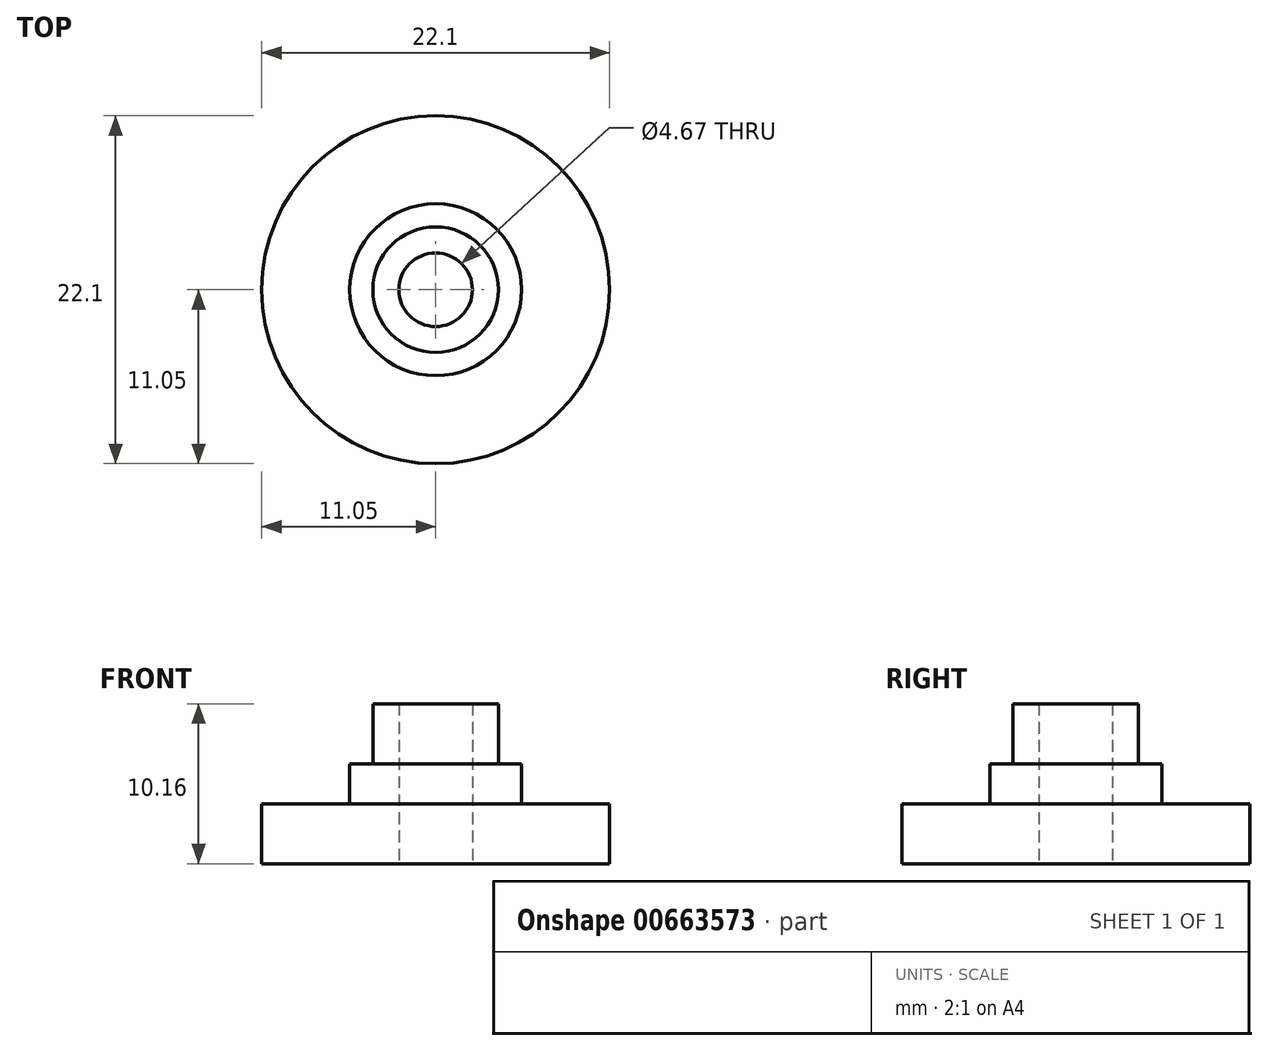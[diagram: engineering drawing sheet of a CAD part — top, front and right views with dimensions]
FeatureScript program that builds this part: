
annotation { "Feature Type Name" : "Feature", "Feature Type Description" : "" }
export const myFeature = defineFeature(function(context is Context, id is Id, definition is map)
    precondition{}
    {
        {
            var Q0;
            Q0=qCreatedBy(makeId("Top.planeOp"),FACE);
            var sketch = newSketch(context, id + "F0", { "sketchPlane" : qUnion([Q0])});
            skCircle(sketch, "E0", {"center": v(0, 0) * mm, "radius": 11.05 * mm});
            skCircle(sketch, "E1", {"center": v(0, 0) * mm, "radius": 2.34 * mm});
            skSolve(sketch);
        }
        {
            var Q0;
            Q0 = qSketchRegion(id + "F0", true);
            extrude(context, id + "F1", {"entities" : qUnion([Q0]), "depth" : 3.8 * mm, "offsetDistance" : 25.4 * mm});
        }
        {
            var Q0;
            Q0=qCreatedBy(makeId("Top.planeOp"),FACE);
            var sketch = newSketch(context, id + "F2", { "sketchPlane" : qUnion([Q0])});
            skCircle(sketch, "E2", {"center": v(0, 0) * mm, "radius": 5.46 * mm});
            skCircle(sketch, "E3", {"center": v(0, 0) * mm, "radius": 2.34 * mm});
            skSolve(sketch);
        }
        {
            var Q0;
            Q0 = qSketchRegion(id + "F2", true);
            extrude(context, id + "F3", {"entities" : qUnion([Q0]), "operationType" : NewBodyOperationType.ADD, "depth" : 6.35 * mm, "offsetDistance" : 25.4 * mm});
        }
        {
            var Q0;
            Q0=qCreatedBy(makeId("Top.planeOp"),FACE);
            var sketch = newSketch(context, id + "F4", { "sketchPlane" : qUnion([Q0])});
            skCircle(sketch, "E4", {"center": v(0, 0) * mm, "radius": 3.99 * mm});
            skCircle(sketch, "E5", {"center": v(0, 0) * mm, "radius": 2.34 * mm});
            skSolve(sketch);
        }
        {
            var Q0;
            Q0 = qSketchRegion(id + "F4", true);
            extrude(context, id + "F5", {"entities" : qUnion([Q0]), "operationType" : NewBodyOperationType.ADD, "depth" : 10.16 * mm, "offsetDistance" : 25.4 * mm});
        }
    });
